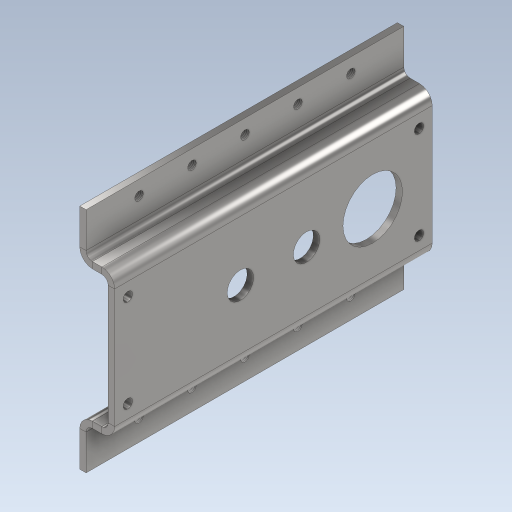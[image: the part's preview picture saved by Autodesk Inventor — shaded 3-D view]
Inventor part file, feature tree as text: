
AUTODESK INVENTOR PART (.ipt)
format: ipt  version: 2023 (Build 270158000, 158)  size: 300,544 bytes
history: native  units: in
note: dims shown in document units (in); Inventor stores cm internally (conversion verified against a paired STEP export)
features: sheet_metal_op x15, sketch x7, other x6, hole x2, projected_geometry x2
ambient origin geometry x8: Origin, YZ Plane, XZ Plane, XY Plane, X Axis, Y Axis, Z Axis, Center Point
bodies: Body1 (feature_tree)
feature tree (32):
  sheet_metal_op  "Face2"
  sheet_metal_op  "Flange1"
  sheet_metal_op  "Flange4"
  hole  "Hole2"  [1 undecoded]
  hole  "Hole1"  [1 undecoded]
  sheet_metal_op  "Face3"
  sheet_metal_op  "Flange2"
  sheet_metal_op  "Flange3"
  other  "Plate2"
  sketch  "Sketch2"  dims[d0=2.25in d1=6.0in]
  other  "Plate3"
  sheet_metal_op  "Bend1"
  sheet_metal_op  "Corner1"
  sketch  "Sketch3"  dims[d3=1.25in d4=1.25in]
  projected_geometry  "Projected Loop1"
  sketch  "Sketch4"  dims[d7=0.5in]
  other  "Plate4"
  sheet_metal_op  "Bend2"
  sketch  "Sketch5"  dims[d8=1.125in]
  other  "Plate5"
  sheet_metal_op  "Bend3"
  sheet_metal_op  "Corner2"
  sketch  "Sketch6"  dims[d10=0.12in]
  other  "Plate6"
  sheet_metal_op  "Bend4"
  sheet_metal_op  "Corner3"
  sketch  "Sketch7"  dims[d11=0.177in]
  other  "Plate7"
  sheet_metal_op  "Bend5"
  sheet_metal_op  "Corner4"
  sketch  "Sketch8"  dims[d12=5.5in d13=1.75in d14=0.5in d15=6.0in d16=0.5in d17=6.0in d18=0.12in d19=0.06in d20=0.24in d21=0.12in d22=0.6583in d23=90.0deg d24=0.12in d25=0.48in d26=0.12in d27=0.12in d28=1.0in d29=1.9685in d31=1.0in d32=0.3937in d34=1.0in d36=0.1628in d37=5.0in d38=0.22in d39=0.44in d40=0.5635in d41=0.12in d42=0.8108in d44=3.75in d45=15.748in d46=0.12in d47=0.12in d48=0.06in d49=0.24in d50=0.12in d51=0.12in d52=0.06in d53=0.24in d54=0.12in d55=0.75in d56=90.0deg d57=0.12in d58=0.48in d59=0.12in d60=0.12in d61=0.12in d62=0.06in d63=0.24in d64=0.12in d65=0.75in d66=90.0deg d67=0.12in d68=0.48in d69=0.12in d70=0.12in d71=0.75in d72=0.75in d73=0.75in d74=1.125in d75=0.5in d76=1.125in d77=1.5748in d79=2.25in d80=0.3937in d82=1.0in d84=0.12in d85=0.06in d86=0.24in d87=0.12in d88=0.7874in d89=90.0deg d90=0.12in d91=0.48in d92=0.12in d93=0.12in d94=0.3937in d95=1.0in d96=1.9685in d98=1.0in d99=0.3937in d101=1.0in d103=0.1628in d104=5.0in d105=0.375in d106=0.25in d107=0.5635in d108=1.0in d109=0.8108in d110=0.3937in d112=1.0in d113=0.7874in d115=3.6374in]
  projected_geometry  "Projected Loop2"
note: 2 required parameter values undecoded (feature->parameter linkage not recoverable at this tier; creation-order binding heuristic only, values carry confidence <= 0.55)
